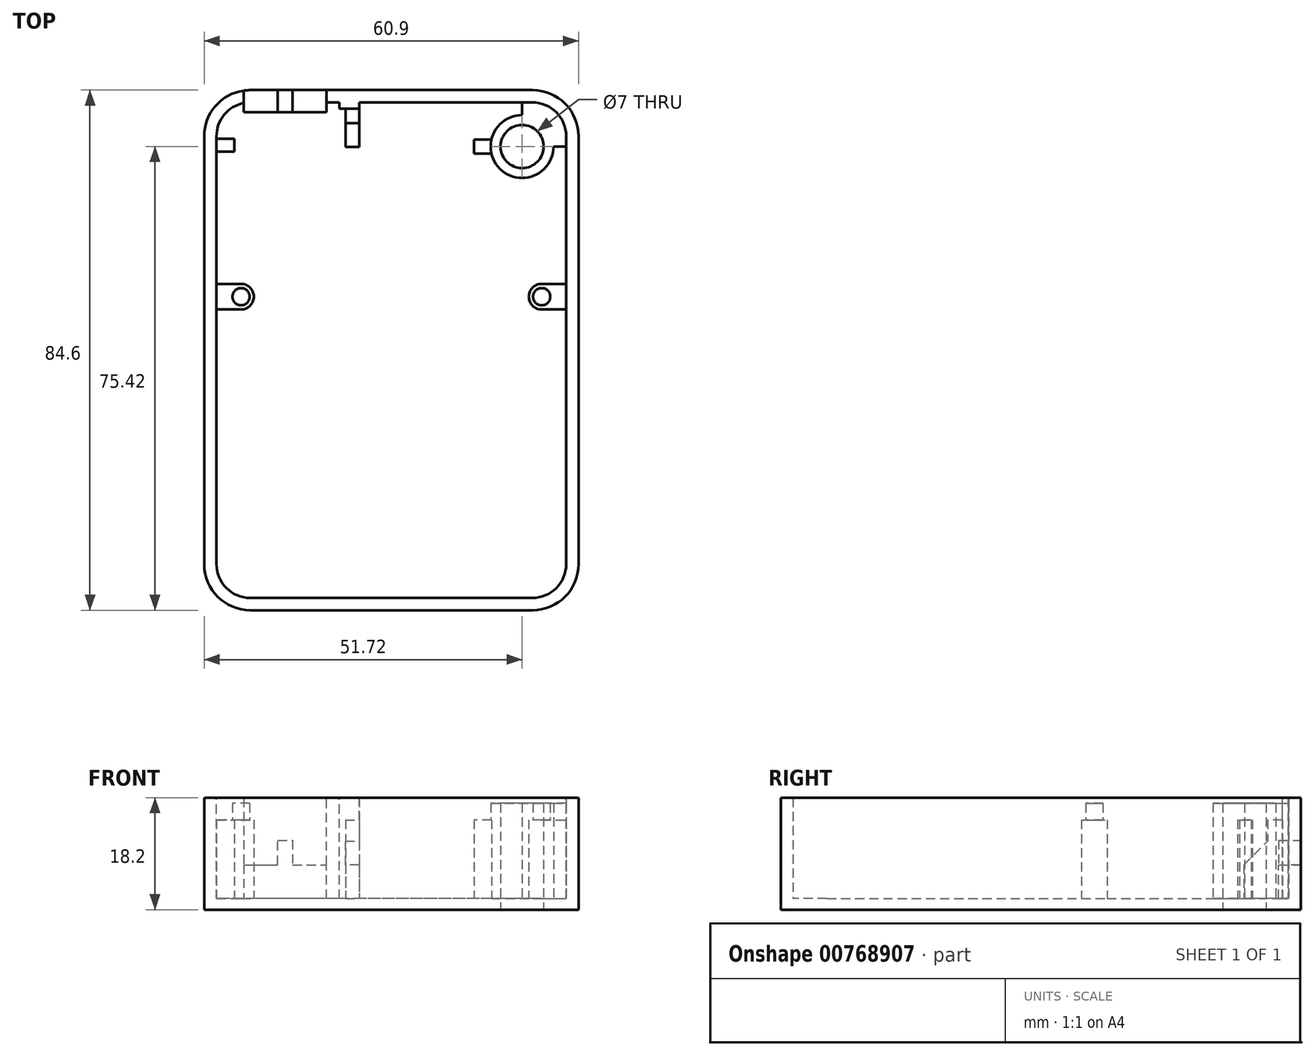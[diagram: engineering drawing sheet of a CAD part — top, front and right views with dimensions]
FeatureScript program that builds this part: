
annotation { "Feature Type Name" : "Feature", "Feature Type Description" : "" }
export const myFeature = defineFeature(function(context is Context, id is Id, definition is map)
    precondition{}
    {
        {
            var Q0;
            Q0=qCreatedBy(makeId("Top.planeOp"),FACE);
            var sketch = newSketch(context, id + "F0", { "sketchPlane" : qUnion([Q0])});
            skLineSegment(sketch, "E0.bottom", {"start": v(22.95, -42.3) * mm, "end": v(-22.95, -42.3) * mm});
            skLineSegment(sketch, "E0.top", {"start": v(22.95, 42.3) * mm, "end": v(-22.95, 42.3) * mm});
            skLineSegment(sketch, "E0.left", {"start": v(30.45, -34.8) * mm, "end": v(30.45, 34.8) * mm});
            skLineSegment(sketch, "E0.right", {"start": v(-30.45, -34.8) * mm, "end": v(-30.45, 34.8) * mm});
            skPoint(sketch, "E0.middle", {"position": v(0, 0) * mm});
            skPoint(sketch, "E1.visualSharp", {"position": v(-30.45, 42.3) * mm});
            skArc(sketch, "E1.filletArc", {"start": v(-22.95, 42.3) * mm, "mid": v(-28.25, 40.1) * mm, "end": v(-30.45, 34.8) * mm});
            skPoint(sketch, "E2.visualSharp", {"position": v(30.45, 42.3) * mm});
            skArc(sketch, "E2.filletArc", {"start": v(30.45, 34.8) * mm, "mid": v(28.25, 40.1) * mm, "end": v(22.95, 42.3) * mm});
            skPoint(sketch, "E3.visualSharp", {"position": v(30.45, -42.3) * mm});
            skArc(sketch, "E3.filletArc", {"start": v(22.95, -42.3) * mm, "mid": v(28.25, -40.1) * mm, "end": v(30.45, -34.8) * mm});
            skPoint(sketch, "E4.visualSharp", {"position": v(-30.45, -42.3) * mm});
            skArc(sketch, "E4.filletArc", {"start": v(-30.45, -34.8) * mm, "mid": v(-28.25, -40.1) * mm, "end": v(-22.95, -42.3) * mm});
            skSolve(sketch);
        }
        {
            var Q0;
            Q0 = qSketchRegion(id + "F0", true);
            extrude(context, id + "F1", {"entities" : qUnion([Q0]), "depth" : 18.4 * mm, "offsetDistance" : 25 * mm});
        }
        {
            var Q0;
            Q0=makeQuery(id+"F1.opExtrude","CAP_FACE",FACE,{"disambiguationData":[OSD([sQuery(id+"F0.wireOp",EDGE,"E0.bottom"),sQuery(id+"F0.wireOp",EDGE,"E0.top"),sQuery(id+"F0.wireOp",EDGE,"E0.left"),sQuery(id+"F0.wireOp",EDGE,"E0.right"),sQuery(id+"F0.wireOp",EDGE,"E1.filletArc"),sQuery(id+"F0.wireOp",EDGE,"E2.filletArc"),sQuery(id+"F0.wireOp",EDGE,"E3.filletArc"),sQuery(id+"F0.wireOp",EDGE,"E4.filletArc")])],"isStart":false});
            shell(context, id + "F2", {"entities" : qUnion([Q0]), "thickness" : 2 * mm});
        }
        {
            var Q0;
            Q0=makeQuery(id+"F1.opExtrude","CAP_FACE",FACE,{"disambiguationData":[OSD([sQuery(id+"F0.wireOp",EDGE,"E0.bottom"),sQuery(id+"F0.wireOp",EDGE,"E0.top"),sQuery(id+"F0.wireOp",EDGE,"E0.left"),sQuery(id+"F0.wireOp",EDGE,"E0.right"),sQuery(id+"F0.wireOp",EDGE,"E1.filletArc"),sQuery(id+"F0.wireOp",EDGE,"E2.filletArc"),sQuery(id+"F0.wireOp",EDGE,"E3.filletArc"),sQuery(id+"F0.wireOp",EDGE,"E4.filletArc")])],"isStart":true});
            extrude(context, id + "F3", {"entities" : qUnion([Q0]), "operationType" : NewBodyOperationType.REMOVE, "oppositeDirection" : true, "depth" : 0.2 * mm, "offsetDistance" : 25 * mm});
        }
        {
            var Q0;
            Q0=makeQuery(id+"F2.opShell","OFFSET_FACE",FACE,{"disambiguationData":[OSD([sQuery(id+"F0.wireOp",EDGE,"E0.bottom"),sQuery(id+"F0.wireOp",EDGE,"E0.top"),sQuery(id+"F0.wireOp",EDGE,"E0.left"),sQuery(id+"F0.wireOp",EDGE,"E0.right"),sQuery(id+"F0.wireOp",EDGE,"E1.filletArc"),sQuery(id+"F0.wireOp",EDGE,"E2.filletArc"),sQuery(id+"F0.wireOp",EDGE,"E3.filletArc"),sQuery(id+"F0.wireOp",EDGE,"E4.filletArc")])]});
            var sketch = newSketch(context, id + "F4", { "sketchPlane" : qUnion([Q0])});
            skCircle(sketch, "E5", {"center": v(-24.45, 8.7) * mm, "radius": 1.4 * mm});
            skCircle(sketch, "E6", {"center": v(24.45, 8.7) * mm, "radius": 1.4 * mm});
            skArc(sketch, "E7", {"start": v(-24.45, 10.78) * mm, "mid": v(-22.37, 8.7) * mm, "end": v(-24.45, 6.62) * mm});
            skLineSegment(sketch, "E8", {"start": v(-24.45, 10.78) * mm, "end": v(-28.45, 10.78) * mm});
            skLineSegment(sketch, "E9", {"start": v(-24.45, 6.62) * mm, "end": v(-28.45, 6.62) * mm});
            skLineSegment(sketch, "E10", {"start": v(-24.45, 8.7) * mm, "end": v(24.45, 8.7) * mm, "construction": true});
            skArc(sketch, "E11", {"start": v(24.45, 6.62) * mm, "mid": v(22.37, 8.7) * mm, "end": v(24.45, 10.78) * mm});
            skLineSegment(sketch, "E12", {"start": v(24.45, 10.78) * mm, "end": v(28.45, 10.78) * mm});
            skLineSegment(sketch, "E13", {"start": v(24.45, 6.62) * mm, "end": v(28.45, 6.62) * mm});
            skCircle(sketch, "E14", {"center": v(21.27, 33.12) * mm, "radius": 3.5 * mm});
            skLineSegment(sketch, "E15", {"start": v(16.29, 32) * mm, "end": v(13.45, 32) * mm});
            skLineSegment(sketch, "E16", {"start": v(13.45, 32) * mm, "end": v(13.45, 34.24) * mm});
            skLineSegment(sketch, "E17", {"start": v(13.45, 34.24) * mm, "end": v(16.29, 34.24) * mm});
            skLineSegment(sketch, "E18", {"start": v(21.27, 33.12) * mm, "end": v(13.45, 33.12) * mm, "construction": true});
            skLineSegment(sketch, "E19", {"start": v(21.27, 33.12) * mm, "end": v(21.27, 38.23) * mm, "construction": true});
            skLineSegment(sketch, "E20", {"start": v(21.27, 38.23) * mm, "end": v(21.27, 40.3) * mm});
            skLineSegment(sketch, "E21", {"start": v(21.27, 33.12) * mm, "end": v(26.38, 33.12) * mm, "construction": true});
            skLineSegment(sketch, "E22", {"start": v(26.38, 33.12) * mm, "end": v(28.45, 33.12) * mm});
            skArc(sketch, "E23", {"start": v(26.38, 33.12) * mm, "mid": v(24.88, 36.73) * mm, "end": v(21.27, 38.23) * mm, "construction": true});
            skArc(sketch, "E24", {"start": v(21.27, 38.23) * mm, "mid": v(17.66, 29.5) * mm, "end": v(26.38, 33.12) * mm});
            skLineSegment(sketch, "E25", {"start": v(-7.45, 40.3) * mm, "end": v(-7.45, 36.9) * mm});
            skLineSegment(sketch, "E26", {"start": v(-7.45, 36.9) * mm, "end": v(-5.25, 36.9) * mm});
            skLineSegment(sketch, "E27", {"start": v(-5.25, 36.9) * mm, "end": v(-5.25, 40.3) * mm});
            skLineSegment(sketch, "E28", {"start": v(-28.45, 34.4) * mm, "end": v(-25.55, 34.4) * mm});
            skLineSegment(sketch, "E29", {"start": v(-25.55, 34.4) * mm, "end": v(-25.55, 32.3) * mm});
            skLineSegment(sketch, "E30", {"start": v(-25.55, 32.3) * mm, "end": v(-28.45, 32.3) * mm});
            skLineSegment(sketch, "E31", {"start": v(-7.45, 36.9) * mm, "end": v(-7.45, 33.05) * mm});
            skLineSegment(sketch, "E32", {"start": v(-7.45, 33.05) * mm, "end": v(-5.25, 33.05) * mm});
            skLineSegment(sketch, "E33", {"start": v(-5.25, 33.05) * mm, "end": v(-5.25, 36.9) * mm});
            skSolve(sketch);
        }
        {
            var Q0;
            Q0=makeQuery(id+"F4.imprint","IMPRINT",FACE,{"disambiguationData":[TD([[makeQuery(id+"F4.imprint","IMPRINT",EDGE,{"derivedFrom":sQuery(id+"F4.wireOp",EDGE,"E6")}),-1.0]])]});
            var Q1;
            Q1=makeQuery(id+"F4.imprint","IMPRINT",FACE,{"disambiguationData":[TD([[makeQuery(id+"F4.imprint","IMPRINT",EDGE,{"derivedFrom":sQuery(id+"F4.wireOp",EDGE,"E5")}),-1.0]])]});
            var Q2;
            {var subQ0=sQuery(id+"F4.wireOp",EDGE,"E28");Q2=makeQuery(id+"F4.imprint","IMPRINT",FACE,{"disambiguationData":[TD([[makeQuery(id+"F4.imprint","IMPRINT",EDGE,{"derivedFrom":subQ0}),-1.0]])]});}
            var Q3;
            {var subQ0=sQuery(id+"F4.wireOp",EDGE,"E25");Q3=makeQuery(id+"F4.imprint","IMPRINT",FACE,{"disambiguationData":[TD([[makeQuery(id+"F4.imprint","IMPRINT",EDGE,{"derivedFrom":subQ0}),1.0]])]});}
            var Q4;
            {var subQ0=sQuery(id+"F4.wireOp",EDGE,"E15");Q4=makeQuery(id+"F4.imprint","IMPRINT",FACE,{"disambiguationData":[TD([[makeQuery(id+"F4.imprint","IMPRINT",EDGE,{"derivedFrom":subQ0}),-1.0]])]});}
            extrude(context, id + "F5", {"entities" : qUnion([Q0, Q1, Q2, Q3, Q4]), "operationType" : NewBodyOperationType.ADD, "depth" : 12.8 * mm, "offsetDistance" : 25 * mm});
        }
        {
            var Q0;
            Q0=makeQuery(id+"F4.imprint","IMPRINT",FACE,{"disambiguationData":[TD([[makeQuery(id+"F4.imprint","IMPRINT",EDGE,{"derivedFrom":sQuery(id+"F4.wireOp",EDGE,"E14")}),-1.0]])]});
            var Q1;
            Q1=makeQuery(id+"F4.imprint","IMPRINT",FACE,{"disambiguationData":[TD([[makeQuery(id+"F4.imprint","IMPRINT",EDGE,{"derivedFrom":sQuery(id+"F4.wireOp",EDGE,"E6")}),1.0]])]});
            var Q2;
            Q2=makeQuery(id+"F4.imprint","IMPRINT",FACE,{"disambiguationData":[TD([[makeQuery(id+"F4.imprint","IMPRINT",EDGE,{"derivedFrom":sQuery(id+"F4.wireOp",EDGE,"E5")}),1.0]])]});
            extrude(context, id + "F6", {"entities" : qUnion([Q0, Q1, Q2]), "operationType" : NewBodyOperationType.ADD, "depth" : 15.5 * mm, "offsetDistance" : 25 * mm});
        }
        {
            var Q0;
            Q0=makeQuery(id+"F4.imprint","IMPRINT",FACE,{"disambiguationData":[TD([[makeQuery(id+"F4.imprint","IMPRINT",EDGE,{"derivedFrom":sQuery(id+"F4.wireOp",EDGE,"E26")}),-1.0]])]});
            extrude(context, id + "F7", {"entities" : qUnion([Q0]), "operationType" : NewBodyOperationType.ADD, "depth" : 9.5 * mm, "offsetDistance" : 25 * mm});
        }
        {
            var Q0;
            Q0=makeQuery(id+"F7.opExtrude","CAP_EDGE",EDGE,{"disambiguationData":[OSD([sQuery(id+"F4.wireOp",EDGE,"E32")])],"isStart":false});
            chamfer(context, id + "F8", {"entities" : qUnion([Q0]), "width" : 4 * mm, "tangentPropagation" : true});
        }
        {
            var Q0;
            Q0=makeQuery(id+"F4.imprint","IMPRINT",FACE,{"disambiguationData":[TD([[makeQuery(id+"F4.imprint","IMPRINT",EDGE,{"derivedFrom":sQuery(id+"F4.wireOp",EDGE,"E14")}),1.0]])]});
            extrude(context, id + "F9", {"entities" : qUnion([Q0]), "operationType" : NewBodyOperationType.REMOVE, "endBound" : BoundingType.THROUGH_ALL, "oppositeDirection" : true, "depth" : 25 * mm, "offsetDistance" : 25 * mm});
        }
        {
            var Q0;
            Q0=makeQuery(id+"F2.opShell","OFFSET_FACE",FACE,{"disambiguationData":[OSD([sQuery(id+"F0.wireOp",EDGE,"E0.top")])]});
            var sketch = newSketch(context, id + "F10", { "sketchPlane" : qUnion([Q0])});
            skLineSegment(sketch, "E34.bottom", {"start": v(-5.25, 2) * mm, "end": v(-8.45, 2) * mm});
            skLineSegment(sketch, "E34.top", {"start": v(-5.25, 18.4) * mm, "end": v(-8.45, 18.4) * mm});
            skLineSegment(sketch, "E34.left", {"start": v(-5.25, 2) * mm, "end": v(-5.25, 18.4) * mm});
            skLineSegment(sketch, "E34.right", {"start": v(-8.45, 2) * mm, "end": v(-8.45, 18.4) * mm});
            skLineSegment(sketch, "E35.bottom", {"start": v(-10.55, 2) * mm, "end": v(-24, 2) * mm});
            skLineSegment(sketch, "E35.left", {"start": v(-10.55, 2) * mm, "end": v(-10.55, 7.5) * mm});
            skLineSegment(sketch, "E35.right", {"start": v(-24, 2) * mm, "end": v(-24, 7.5) * mm});
            skLineSegment(sketch, "E36.0", {"start": v(28.45, 17.5) * mm, "end": v(28.45, 2) * mm, "construction": true});
            skLineSegment(sketch, "E37.top", {"start": v(-24, 18.4) * mm, "end": v(-10.55, 18.4) * mm});
            skLineSegment(sketch, "E37.left", {"start": v(-24, 7.5) * mm, "end": v(-24, 18.4) * mm});
            skLineSegment(sketch, "E37.right", {"start": v(-10.55, 7.5) * mm, "end": v(-10.55, 18.4) * mm});
            skLineSegment(sketch, "E38", {"start": v(-18.47, 7.5) * mm, "end": v(-16.07, 7.5) * mm, "construction": true});
            skLineSegment(sketch, "E39", {"start": v(-16.07, 7.5) * mm, "end": v(-10.55, 7.5) * mm});
            skLineSegment(sketch, "E40", {"start": v(-24, 7.5) * mm, "end": v(-18.47, 7.5) * mm});
            skLineSegment(sketch, "E41", {"start": v(-10.55, 2) * mm, "end": v(-8.45, 2) * mm, "construction": true});
            skLineSegment(sketch, "E42", {"start": v(-18.47, 7.5) * mm, "end": v(-18.47, 11.5) * mm});
            skLineSegment(sketch, "E43", {"start": v(-18.47, 11.5) * mm, "end": v(-16.07, 11.5) * mm});
            skLineSegment(sketch, "E44", {"start": v(-16.07, 11.5) * mm, "end": v(-16.07, 7.5) * mm});
            skLineSegment(sketch, "E45.0", {"start": v(-28.45, 18.4) * mm, "end": v(-28.45, 2) * mm, "construction": true});
            skSolve(sketch);
        }
        {
            var Q0;
            {var subQ4=sQuery(id+"F10.wireOp",EDGE,"E34.top");Q0=makeQuery(id+"F10.imprint","IMPRINT",FACE,{"disambiguationData":[TD([[makeQuery(id+"F10.imprint","IMPRINT",EDGE,{"derivedFrom":subQ4}),1.0]])]});}
            extrude(context, id + "F11", {"entities" : qUnion([Q0]), "operationType" : NewBodyOperationType.ADD, "depth" : 1 * mm, "offsetDistance" : 25 * mm});
        }
        {
            var Q0;
            {var subQ8=sQuery(id+"F10.wireOp",EDGE,"E35.left");Q0=makeQuery(id+"F10.imprint","IMPRINT",FACE,{"disambiguationData":[TD([[makeQuery(id+"F10.imprint","IMPRINT",EDGE,{"derivedFrom":subQ8}),1.0]])]});}
            var Q1;
            {var subQ3=sQuery(id+"F10.wireOp",EDGE,"E35.right");Q1=makeQuery(id+"F10.imprint","IMPRINT",FACE,{"disambiguationData":[TD([[makeQuery(id+"F10.imprint","IMPRINT",EDGE,{"derivedFrom":subQ3}),-1.0]])]});}
            extrude(context, id + "F12", {"entities" : qUnion([Q0, Q1]), "operationType" : NewBodyOperationType.ADD, "depth" : 1.6 * mm, "offsetDistance" : 25 * mm});
        }
        {
            var Q0;
            {var subQ0=sQuery(id+"F10.wireOp",EDGE,"E37.right");Q0=makeQuery(id+"F10.imprint","IMPRINT",FACE,{"disambiguationData":[TD([[makeQuery(id+"F10.imprint","IMPRINT",EDGE,{"derivedFrom":subQ0}),1.0]])]});}
            var Q1;
            {var subQ3=sQuery(id+"F10.wireOp",EDGE,"E37.left");Q1=makeQuery(id+"F10.imprint","IMPRINT",FACE,{"disambiguationData":[TD([[makeQuery(id+"F10.imprint","IMPRINT",EDGE,{"derivedFrom":subQ3}),-1.0]])]});}
            extrude(context, id + "F13", {"entities" : qUnion([Q0, Q1]), "operationType" : NewBodyOperationType.REMOVE, "endBound" : BoundingType.SYMMETRIC, "oppositeDirection" : true, "depth" : 6 * mm, "offsetDistance" : 25 * mm});
        }
    });
